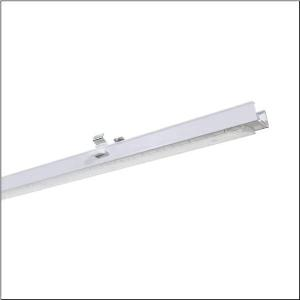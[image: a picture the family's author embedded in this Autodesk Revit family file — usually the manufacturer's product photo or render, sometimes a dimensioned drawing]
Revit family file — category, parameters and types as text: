
# Revit family: trunking_flex_31_51re11ma46b
name_source: partatom
category: Lighting Fixtures
units: mm (PartAtom-declared; Revit-internal decimal feet)

## family parameters
Cut with Voids When Loaded = No
Host = Face
Light Source = No
Part Type = Normal
Room Calculation Point = No
Round Connector Dimension = Use Diameter
Shared = No

## types (1)
- --- (1 x LED, 6400 lm, 40 W, 4000K)
    Apparent Load = 40 VA
    CIE Flux Codes = 83 93 98 100 100
    Color Rendering = 80
    Color Temperature = 4000K
    Default Elevation = 1800 mm
    Description = Trunking Flex 31, luminaire insert, of extruded aluminium section, coated, traffic white (RAL 9016), length: 1.172mm, width: 91mm, height: 53mm, LED rated luminous flux: 6.400lm, light colour: 840, control gear: ON/OFF Multilumen, with system connector: socket, mains connection: 220..240V, AC, 50/60Hz, rated input power: 40W, luminous flux adjustable on luminaire in four steps (3420/4540/5580/6630lm), connected load according to luminous flux setting (20/26/33/40W), primary light control with lens, of plastic, primary optical cover: cover, of PMMA, light emission: direct distribution, protection rating (complete): IP20, insulation class (complete): insulation class I (protective earthing), certification: CE, UKCA, impact resistance: IK02, permissible ambient temperature for indoor applications: -20..+40°C, packaging unit: 1 piece
    Height = 58 mm
    Lamp = 1 x LED
    Lamp Light Flux = 6400 lm
    Lamp Power = 40 W
    Lamp count = 1
    Length = 1172 mm
    Luminous efficacy = 160 lm/W
    Manufacturer = Siteco
    ModVariant = No
    Model = 51RE11MA46B
    Mounting Place = Ceiling
    Mounting Type = Pendant
    Number of Poles = 1
    OnlyDefault = Yes
    Power Factor = 1
    Product Name = Trunking Flex 31
    Product group = luminaire insert
    ProductGroupID = 901
    Protection Class = Protection class I
    Protection Degree = IP 20
    RLX_Detail_Level = 1
    RLX_Emergency_Light_Flux = 0 lm
    RLX_Emergency_Type = 0
    RLX_Emergency_Type_DB = No
    RlxData = <blob elided: 19857 chars, md5=0ee4d47a>
    Socket = socket
    Standby Power = 0 W
    System Light Flux = 6400 lm
    System Power = 40 W
    Type Comments = factory setting: luminous flux: 100 % | (ON | ON) | 300 mA
    Type Image = l_1266702.jpg
    URL = http://relux.com
    VarID = @adj_001415
    Voltage = 0 V
    Weight = 0.00 kg
    Width = 65 mm

## geometry (parser evidence)
native form markers: Blend x4, Sweep x12
no freeform markers — native parametric forms only
